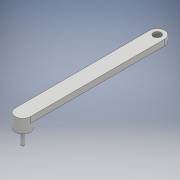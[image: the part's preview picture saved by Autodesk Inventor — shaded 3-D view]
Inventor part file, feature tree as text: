
AUTODESK INVENTOR PART (.ipt)
format: ipt  version: 2017 (Build 210142000, 142)  size: 257,024 bytes
history: native  units: mm
features: extrude x5, sketch x5, chamfer x2, hole x1, plane x1, reference x1
ambient origin geometry x8: Origin, YZ Plane, XZ Plane, XY Plane, X Axis, Y Axis, Z Axis, Center Point
bodies: Solid1 (feature_tree)
feature tree (15):
  extrude  "Extrusion1"  Depth=4.5mm
  extrude  "Extrusion2"  Depth=7.0mm TaperAngle=0.0deg
  hole  "Hole1"  [1 undecoded]
  extrude  "Extrusion3"  Depth=9.0mm
  sketch  "Sketch4"  dims[d9=9.0mm d10=6.0mm d11=4.0mm d12=2.0mm d13=90.0deg d14=8.0mm d15=20.594885mm d26=6.0mm]
  plane  "Work Plane1"
  extrude  "Extrusion4"  Depth=1.0mm
  extrude  "Extrusion5"  Depth=1.0mm TaperAngle=0.0deg
  chamfer  "Chamfer1"  Distance=6.0mm
  chamfer  "Chamfer2"  Distance=1.0mm
  sketch  "Sketch1"  dims[d0=4.5mm d1=160.0mm]
  reference  "Reference1"
  sketch  "Sketch2"  dims[d2=18.0mm d3=7.0mm d4=0.0mm]
  sketch  "Sketch3"  dims[d5=9.0mm d6=0.0mm d7=10.0mm d8=10.0mm]
  sketch  "Sketch5"  dims[d27=1.0mm d28=0.0mm d29=3.9mm d30=1.0mm d31=0.0mm d32=6.0mm d33=1.0mm d34=0.0mm d35=1.5mm d36=2.0mm d37=45.0deg d38=0.8mm d39=2.0mm d40=45.0deg]
note: 1 required parameter value undecoded (feature->parameter linkage not recoverable at this tier; creation-order binding heuristic only, values carry confidence <= 0.55)
